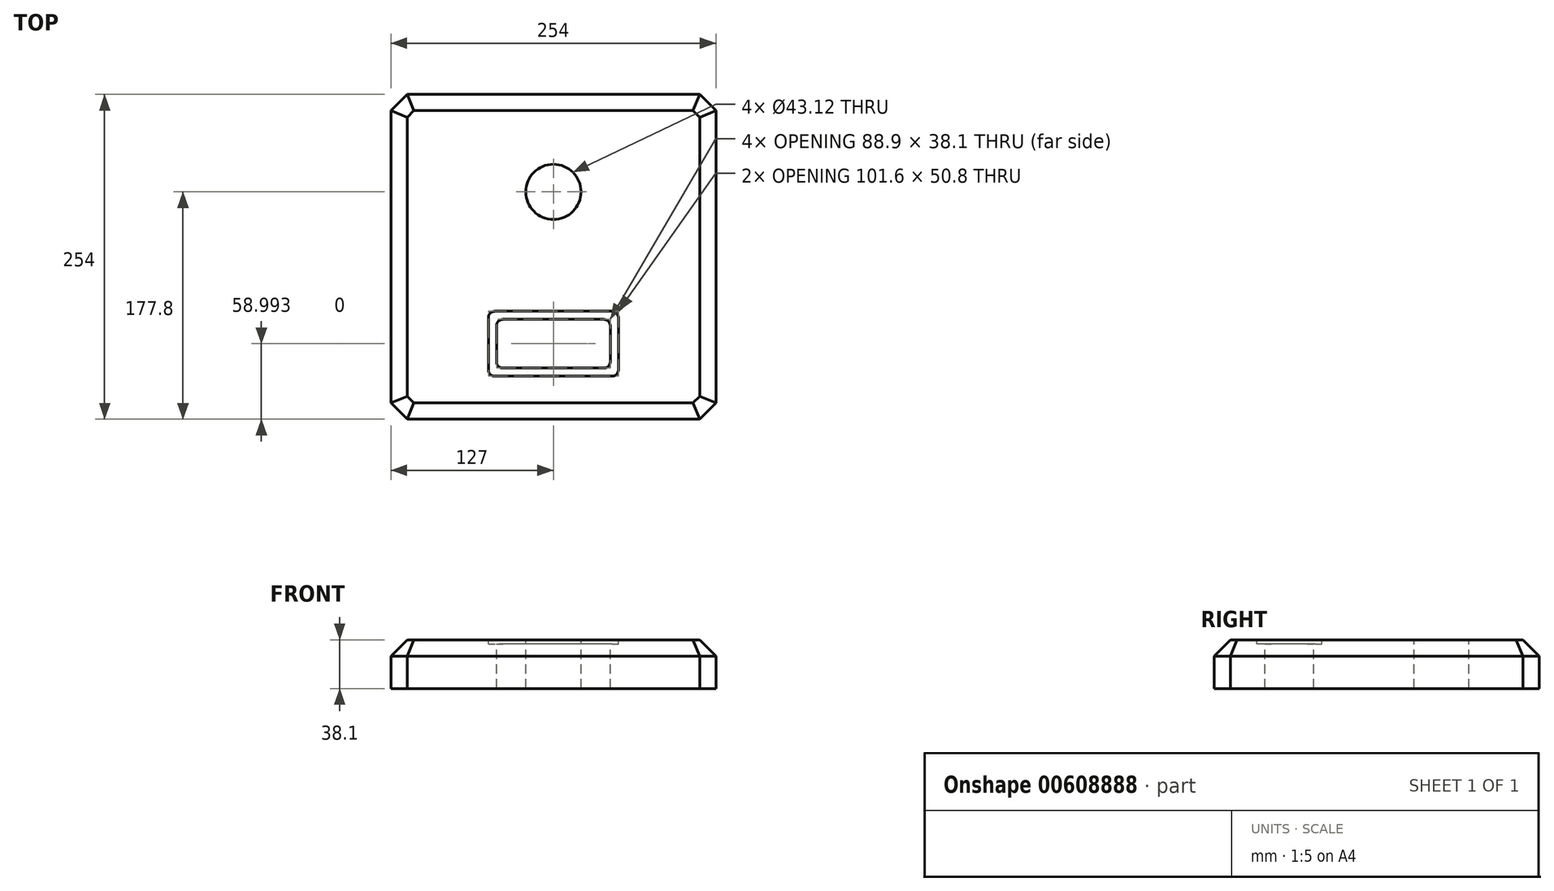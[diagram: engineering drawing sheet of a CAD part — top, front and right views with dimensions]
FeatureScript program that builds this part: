
annotation { "Feature Type Name" : "Feature", "Feature Type Description" : "" }
export const myFeature = defineFeature(function(context is Context, id is Id, definition is map)
    precondition{}
    {
        {
            var Q0;
            Q0=qCreatedBy(makeId("Top.planeOp"),FACE);
            var sketch = newSketch(context, id + "F0", { "sketchPlane" : qUnion([Q0])});
            skLineSegment(sketch, "E0.bottom", {"start": v(127, 127) * mm, "end": v(-127, 127) * mm});
            skLineSegment(sketch, "E0.top", {"start": v(127, -127) * mm, "end": v(-127, -127) * mm});
            skLineSegment(sketch, "E0.left", {"start": v(127, 127) * mm, "end": v(127, -127) * mm});
            skLineSegment(sketch, "E0.right", {"start": v(-127, 127) * mm, "end": v(-127, -127) * mm});
            skPoint(sketch, "E0.middle", {"position": v(0, 0) * mm});
            skSolve(sketch);
        }
        {
            var Q0;
            Q0=makeQuery(id+"F0.imprint","IMPRINT",FACE,{"disambiguationData":[TD([[makeQuery(id+"F0.imprint","IMPRINT",EDGE,{"derivedFrom":sQuery(id+"F0.wireOp",EDGE,"E0.bottom")}),1.0]])]});
            extrude(context, id + "F1", {"entities" : qUnion([Q0]), "depth" : 38.1 * mm, "offsetDistance" : 25.4 * mm});
        }
        {
            var Q0;
            Q0=makeQuery(id+"F1.opExtrude","SWEPT_EDGE",EDGE,{"disambiguationData":[OSD([sQuery(id+"F0.wireOp",EDGE,"E0.top"),sQuery(id+"F0.wireOp",EDGE,"E0.right")])]});
            var Q1;
            Q1=makeQuery(id+"F1.opExtrude","SWEPT_EDGE",EDGE,{"disambiguationData":[OSD([sQuery(id+"F0.wireOp",EDGE,"E0.top"),sQuery(id+"F0.wireOp",EDGE,"E0.left")])]});
            var Q2;
            Q2=makeQuery(id+"F1.opExtrude","SWEPT_EDGE",EDGE,{"disambiguationData":[OSD([sQuery(id+"F0.wireOp",EDGE,"E0.bottom"),sQuery(id+"F0.wireOp",EDGE,"E0.right")])]});
            var Q3;
            Q3=makeQuery(id+"F1.opExtrude","SWEPT_EDGE",EDGE,{"disambiguationData":[OSD([sQuery(id+"F0.wireOp",EDGE,"E0.bottom"),sQuery(id+"F0.wireOp",EDGE,"E0.left")])]});
            chamfer(context, id + "F2", {"entities" : qUnion([Q0, Q1, Q2, Q3]), "width" : 12.7 * mm, "tangentPropagation" : true});
        }
        {
            var Q0;
            Q0=makeQuery(id+"F1.opExtrude","CAP_FACE",FACE,{"disambiguationData":[OSD([sQuery(id+"F0.wireOp",EDGE,"E0.bottom"),sQuery(id+"F0.wireOp",EDGE,"E0.top"),sQuery(id+"F0.wireOp",EDGE,"E0.left"),sQuery(id+"F0.wireOp",EDGE,"E0.right")])],"isStart":false});
            var sketch = newSketch(context, id + "F3", { "sketchPlane" : qUnion([Q0])});
            skCircle(sketch, "E1", {"center": v(0, 50.8) * mm, "radius": 21.56 * mm});
            skSolve(sketch);
        }
        {
            var Q0;
            Q0=makeQuery(id+"F3.imprint","IMPRINT",FACE,{"disambiguationData":[TD([[makeQuery(id+"F3.imprint","IMPRINT",EDGE,{"derivedFrom":sQuery(id+"F3.wireOp",EDGE,"E1")}),1.0]])]});
            extrude(context, id + "F4", {"entities" : qUnion([Q0]), "operationType" : NewBodyOperationType.REMOVE, "endBound" : BoundingType.UP_TO_NEXT, "oppositeDirection" : true, "depth" : 25.4 * mm, "offsetDistance" : 25.4 * mm});
        }
        {
            var Q0;
            Q0=makeQuery(id+"F1.opExtrude","CAP_FACE",FACE,{"disambiguationData":[OSD([sQuery(id+"F0.wireOp",EDGE,"E0.bottom"),sQuery(id+"F0.wireOp",EDGE,"E0.top"),sQuery(id+"F0.wireOp",EDGE,"E0.left"),sQuery(id+"F0.wireOp",EDGE,"E0.right")])],"isStart":false});
            var sketch = newSketch(context, id + "F5", { "sketchPlane" : qUnion([Q0])});
            skLineSegment(sketch, "E2.bottom", {"start": v(50.8, -42.6) * mm, "end": v(-50.8, -42.6) * mm});
            skLineSegment(sketch, "E2.top", {"start": v(50.8, -93.4) * mm, "end": v(-50.8, -93.4) * mm});
            skLineSegment(sketch, "E2.left", {"start": v(50.8, -42.6) * mm, "end": v(50.8, -93.4) * mm});
            skLineSegment(sketch, "E2.right", {"start": v(-50.8, -42.6) * mm, "end": v(-50.8, -93.4) * mm});
            skPoint(sketch, "E2.middle", {"position": v(0, -68) * mm});
            skSolve(sketch);
        }
        {
            var Q0;
            Q0 = qSketchRegion(id + "F5", true);
            extrude(context, id + "F6", {"entities" : qUnion([Q0]), "operationType" : NewBodyOperationType.REMOVE, "oppositeDirection" : true, "depth" : 3.17 * mm, "offsetDistance" : 25.4 * mm});
        }
        {
            var Q0;
            Q0=makeQuery(id+"F5.imprint","IMPRINT",FACE,{"disambiguationData":[TD([[makeQuery(id+"F5.imprint","IMPRINT",EDGE,{"derivedFrom":sQuery(id+"F5.wireOp",EDGE,"E2.bottom")}),1.0]])]});
            var sketch = newSketch(context, id + "F7", { "sketchPlane" : qUnion([Q0])});
            skLineSegment(sketch, "E3.0", {"start": v(44.45, -48.96) * mm, "end": v(-44.45, -48.96) * mm});
            skLineSegment(sketch, "E3.1", {"start": v(44.45, -48.96) * mm, "end": v(44.45, -87.06) * mm});
            skLineSegment(sketch, "E3.2", {"start": v(44.45, -87.06) * mm, "end": v(-44.45, -87.06) * mm});
            skLineSegment(sketch, "E3.3", {"start": v(-44.45, -48.96) * mm, "end": v(-44.45, -87.06) * mm});
            skSolve(sketch);
        }
        {
            var Q0;
            Q0=makeQuery(id+"F7.imprint","IMPRINT",FACE,{"disambiguationData":[TD([[makeQuery(id+"F7.imprint","IMPRINT",EDGE,{"derivedFrom":sQuery(id+"F7.wireOp",EDGE,"E3.0")}),1.0]])]});
            extrude(context, id + "F8", {"entities" : qUnion([Q0]), "operationType" : NewBodyOperationType.REMOVE, "endBound" : BoundingType.THROUGH_ALL, "oppositeDirection" : true, "depth" : 25.4 * mm, "offsetDistance" : 25.4 * mm});
        }
        {
            var Q0;
            Q0=makeQuery(id+"F6.boolean.opBoolean","COPY",EDGE,{"derivedFrom":makeQuery(id+"F6.opExtrude","SWEPT_EDGE",EDGE,{"disambiguationData":[OSD([sQuery(id+"F5.wireOp",EDGE,"E2.bottom"),sQuery(id+"F5.wireOp",EDGE,"E2.right")])]})});
            var Q1;
            Q1=makeQuery(id+"F8.boolean.opBoolean","COPY",EDGE,{"derivedFrom":makeQuery(id+"F8.opExtrude","SWEPT_EDGE",EDGE,{"disambiguationData":[OSD([sQuery(id+"F7.wireOp",EDGE,"E3.0"),sQuery(id+"F7.wireOp",EDGE,"E3.3")])]})});
            var Q2;
            Q2=makeQuery(id+"F8.boolean.opBoolean","COPY",EDGE,{"derivedFrom":makeQuery(id+"F8.opExtrude","SWEPT_EDGE",EDGE,{"disambiguationData":[OSD([sQuery(id+"F7.wireOp",EDGE,"E3.0"),sQuery(id+"F7.wireOp",EDGE,"E3.1")])]})});
            var Q3;
            Q3=makeQuery(id+"F6.boolean.opBoolean","COPY",EDGE,{"derivedFrom":makeQuery(id+"F6.opExtrude","SWEPT_EDGE",EDGE,{"disambiguationData":[OSD([sQuery(id+"F5.wireOp",EDGE,"E2.bottom"),sQuery(id+"F5.wireOp",EDGE,"E2.left")])]})});
            var Q4;
            Q4=makeQuery(id+"F6.boolean.opBoolean","COPY",EDGE,{"derivedFrom":makeQuery(id+"F6.opExtrude","SWEPT_EDGE",EDGE,{"disambiguationData":[OSD([sQuery(id+"F5.wireOp",EDGE,"E2.top"),sQuery(id+"F5.wireOp",EDGE,"E2.left")])]})});
            var Q5;
            Q5=makeQuery(id+"F8.boolean.opBoolean","COPY",EDGE,{"derivedFrom":makeQuery(id+"F8.opExtrude","SWEPT_EDGE",EDGE,{"disambiguationData":[OSD([sQuery(id+"F7.wireOp",EDGE,"E3.1"),sQuery(id+"F7.wireOp",EDGE,"E3.2")])]})});
            var Q6;
            Q6=makeQuery(id+"F8.boolean.opBoolean","COPY",EDGE,{"derivedFrom":makeQuery(id+"F8.opExtrude","SWEPT_EDGE",EDGE,{"disambiguationData":[OSD([sQuery(id+"F7.wireOp",EDGE,"E3.2"),sQuery(id+"F7.wireOp",EDGE,"E3.3")])]})});
            var Q7;
            Q7=makeQuery(id+"F6.boolean.opBoolean","COPY",EDGE,{"derivedFrom":makeQuery(id+"F6.opExtrude","SWEPT_EDGE",EDGE,{"disambiguationData":[OSD([sQuery(id+"F5.wireOp",EDGE,"E2.top"),sQuery(id+"F5.wireOp",EDGE,"E2.right")])]})});
            fillet(context, id + "F9", {"entities" : qUnion([Q0, Q1, Q2, Q3, Q4, Q5, Q6, Q7]), "radius" : 5.08 * mm, "tangentPropagation" : true, "allowEdgeOverflow" : false});
        }
        {
            var Q0;
            Q0=makeQuery(id+"F1.opExtrude","CAP_EDGE",EDGE,{"disambiguationData":[OSD([sQuery(id+"F0.wireOp",EDGE,"E0.top")])],"isStart":false});
            var Q1;
            {var subQ0=sQuery(id+"F0.wireOp",EDGE,"E0.right");var subQ1=sQuery(id+"F0.wireOp",EDGE,"E0.top");Q1=makeQuery(id+"F2.opChamfer","BLEND_EDGE",EDGE,{"blendedFrom":[makeQuery(id+"F1.opExtrude","SWEPT_EDGE",EDGE,{"disambiguationData":[OSD([subQ1,subQ0])]}),makeQuery(id+"F1.opExtrude","CAP_FACE",FACE,{"disambiguationData":[OSD([sQuery(id+"F0.wireOp",EDGE,"E0.bottom"),subQ1,sQuery(id+"F0.wireOp",EDGE,"E0.left"),subQ0])],"isStart":false})],"blendedInto":[makeQuery(id+"F1.opExtrude","CAP_FACE",FACE,{"disambiguationData":[OSD([sQuery(id+"F0.wireOp",EDGE,"E0.bottom"),subQ1,sQuery(id+"F0.wireOp",EDGE,"E0.left"),subQ0])],"isStart":false})]});}
            var Q2;
            Q2=makeQuery(id+"F1.opExtrude","CAP_EDGE",EDGE,{"disambiguationData":[OSD([sQuery(id+"F0.wireOp",EDGE,"E0.right")])],"isStart":false});
            var Q3;
            {var subQ0=sQuery(id+"F0.wireOp",EDGE,"E0.right");var subQ1=sQuery(id+"F0.wireOp",EDGE,"E0.bottom");Q3=makeQuery(id+"F2.opChamfer","BLEND_EDGE",EDGE,{"blendedFrom":[makeQuery(id+"F1.opExtrude","SWEPT_EDGE",EDGE,{"disambiguationData":[OSD([subQ1,subQ0])]}),makeQuery(id+"F1.opExtrude","CAP_FACE",FACE,{"disambiguationData":[OSD([subQ1,sQuery(id+"F0.wireOp",EDGE,"E0.top"),sQuery(id+"F0.wireOp",EDGE,"E0.left"),subQ0])],"isStart":false})],"blendedInto":[makeQuery(id+"F1.opExtrude","CAP_FACE",FACE,{"disambiguationData":[OSD([subQ1,sQuery(id+"F0.wireOp",EDGE,"E0.top"),sQuery(id+"F0.wireOp",EDGE,"E0.left"),subQ0])],"isStart":false})]});}
            var Q4;
            Q4=makeQuery(id+"F1.opExtrude","CAP_EDGE",EDGE,{"disambiguationData":[OSD([sQuery(id+"F0.wireOp",EDGE,"E0.bottom")])],"isStart":false});
            var Q5;
            {var subQ0=sQuery(id+"F0.wireOp",EDGE,"E0.left");var subQ1=sQuery(id+"F0.wireOp",EDGE,"E0.bottom");Q5=makeQuery(id+"F2.opChamfer","BLEND_EDGE",EDGE,{"blendedFrom":[makeQuery(id+"F1.opExtrude","SWEPT_EDGE",EDGE,{"disambiguationData":[OSD([subQ1,subQ0])]}),makeQuery(id+"F1.opExtrude","CAP_FACE",FACE,{"disambiguationData":[OSD([subQ1,sQuery(id+"F0.wireOp",EDGE,"E0.top"),subQ0,sQuery(id+"F0.wireOp",EDGE,"E0.right")])],"isStart":false})],"blendedInto":[makeQuery(id+"F1.opExtrude","CAP_FACE",FACE,{"disambiguationData":[OSD([subQ1,sQuery(id+"F0.wireOp",EDGE,"E0.top"),subQ0,sQuery(id+"F0.wireOp",EDGE,"E0.right")])],"isStart":false})]});}
            var Q6;
            {var subQ0=sQuery(id+"F0.wireOp",EDGE,"E0.left");var subQ1=sQuery(id+"F0.wireOp",EDGE,"E0.top");Q6=makeQuery(id+"F2.opChamfer","BLEND_EDGE",EDGE,{"blendedFrom":[makeQuery(id+"F1.opExtrude","SWEPT_EDGE",EDGE,{"disambiguationData":[OSD([subQ1,subQ0])]}),makeQuery(id+"F1.opExtrude","CAP_FACE",FACE,{"disambiguationData":[OSD([sQuery(id+"F0.wireOp",EDGE,"E0.bottom"),subQ1,subQ0,sQuery(id+"F0.wireOp",EDGE,"E0.right")])],"isStart":false})],"blendedInto":[makeQuery(id+"F1.opExtrude","CAP_FACE",FACE,{"disambiguationData":[OSD([sQuery(id+"F0.wireOp",EDGE,"E0.bottom"),subQ1,subQ0,sQuery(id+"F0.wireOp",EDGE,"E0.right")])],"isStart":false})]});}
            var Q7;
            Q7=makeQuery(id+"F1.opExtrude","CAP_EDGE",EDGE,{"disambiguationData":[OSD([sQuery(id+"F0.wireOp",EDGE,"E0.left")])],"isStart":false});
            chamfer(context, id + "F10", {"entities" : qUnion([Q0, Q1, Q2, Q3, Q4, Q5, Q6, Q7]), "width" : 12.7 * mm, "tangentPropagation" : true});
        }
    });
